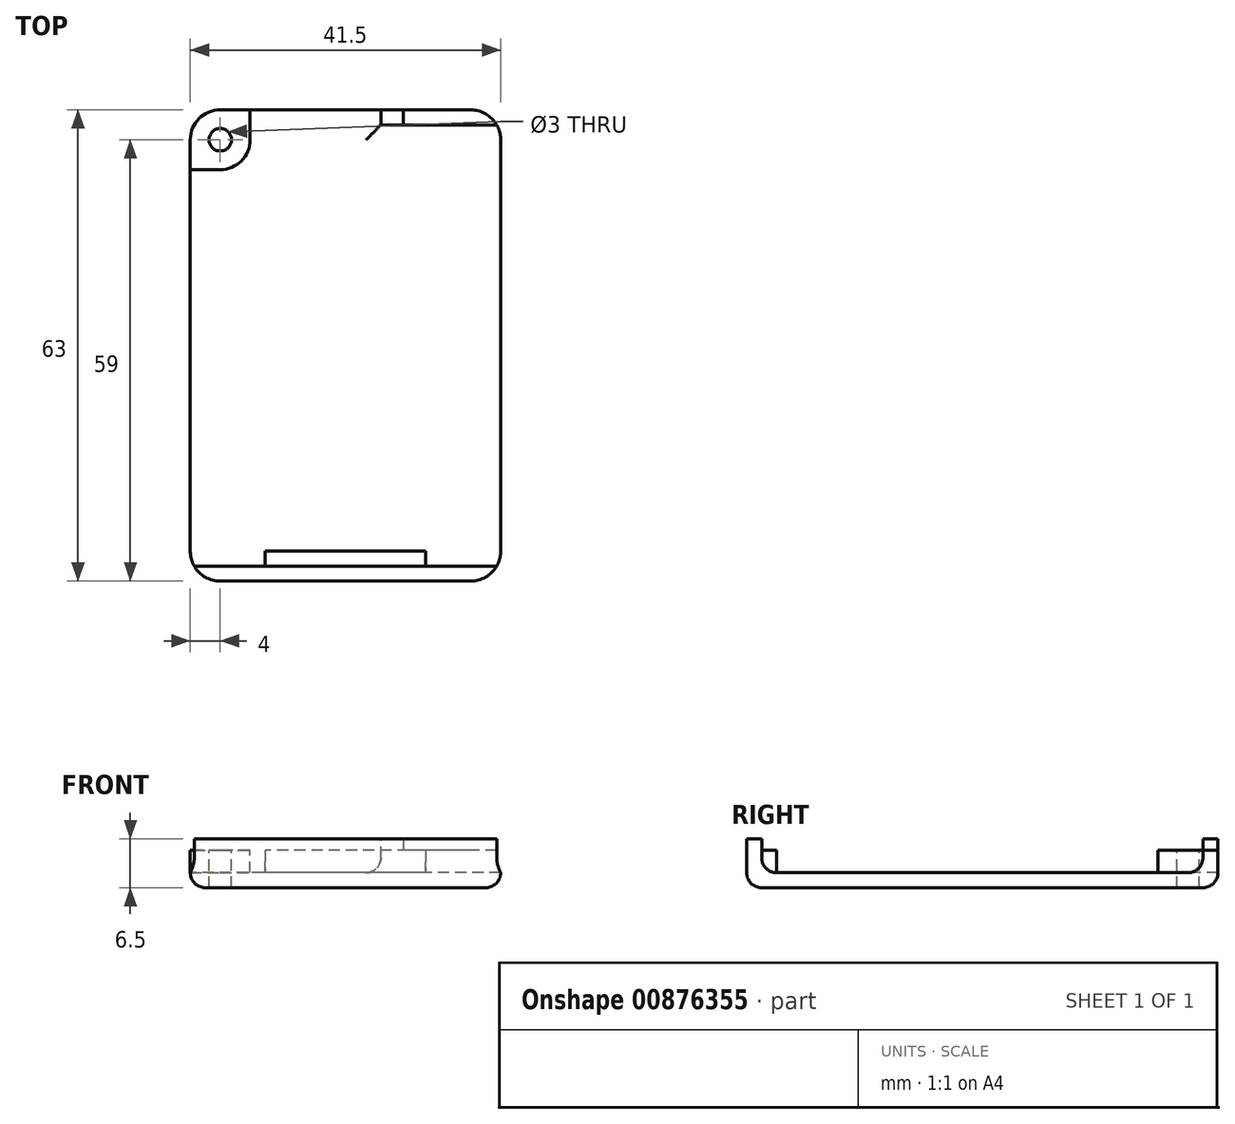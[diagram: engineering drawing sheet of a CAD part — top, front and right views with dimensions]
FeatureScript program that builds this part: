
annotation { "Feature Type Name" : "Feature", "Feature Type Description" : "" }
export const myFeature = defineFeature(function(context is Context, id is Id, definition is map)
    precondition{}
    {
        {
            var Q0;
            Q0=qCreatedBy(makeId("Top.planeOp"),FACE);
            var sketch = newSketch(context, id + "F0", { "sketchPlane" : qUnion([Q0])});
            skLineSegment(sketch, "E0.bottom", {"start": v(20.75, 31.5) * mm, "end": v(-20.75, 31.5) * mm});
            skLineSegment(sketch, "E0.top", {"start": v(20.75, -31.5) * mm, "end": v(-20.75, -31.5) * mm});
            skLineSegment(sketch, "E0.left", {"start": v(20.75, 31.5) * mm, "end": v(20.75, -31.5) * mm});
            skLineSegment(sketch, "E0.right", {"start": v(-20.75, 31.5) * mm, "end": v(-20.75, -31.5) * mm});
            skPoint(sketch, "E0.middle", {"position": v(0, 0) * mm});
            skCircle(sketch, "E1", {"center": v(-16.75, 27.5) * mm, "radius": 1.5 * mm});
            skLineSegment(sketch, "E2.bottom", {"start": v(-20.75, 31.5) * mm, "end": v(-12.75, 31.5) * mm});
            skLineSegment(sketch, "E2.top", {"start": v(-20.75, 23.5) * mm, "end": v(-12.75, 23.5) * mm});
            skLineSegment(sketch, "E2.left", {"start": v(-20.75, 31.5) * mm, "end": v(-20.75, 23.5) * mm});
            skLineSegment(sketch, "E2.right", {"start": v(-12.75, 31.5) * mm, "end": v(-12.75, 23.5) * mm});
            skLineSegment(sketch, "E3.bottom", {"start": v(20.75, 29.5) * mm, "end": v(-20.75, 29.5) * mm});
            skLineSegment(sketch, "E3.top", {"start": v(20.75, -29.5) * mm, "end": v(-20.75, -29.5) * mm});
            skLineSegment(sketch, "E3.left", {"start": v(20.75, 29.5) * mm, "end": v(20.75, -29.5) * mm});
            skLineSegment(sketch, "E3.right", {"start": v(-20.75, 29.5) * mm, "end": v(-20.75, -29.5) * mm});
            skLineSegment(sketch, "E4.bottom", {"start": v(4.75, 31.5) * mm, "end": v(20.75, 31.5) * mm});
            skLineSegment(sketch, "E4.top", {"start": v(4.75, 29.5) * mm, "end": v(20.75, 29.5) * mm});
            skLineSegment(sketch, "E4.left", {"start": v(4.75, 31.5) * mm, "end": v(4.75, 29.5) * mm});
            skLineSegment(sketch, "E4.right", {"start": v(20.75, 31.5) * mm, "end": v(20.75, 29.5) * mm});
            skLineSegment(sketch, "E5.bottom", {"start": v(4.75, 31.5) * mm, "end": v(7.75, 31.5) * mm});
            skLineSegment(sketch, "E5.top", {"start": v(4.75, 29.5) * mm, "end": v(7.75, 29.5) * mm});
            skLineSegment(sketch, "E5.right", {"start": v(7.75, 31.5) * mm, "end": v(7.75, 29.5) * mm});
            skSolve(sketch);
        }
        {
            var Q0;
            {var subQ0=sQuery(id+"F0.wireOp",EDGE,"E5.right");var subQ1=sQuery(id+"F0.wireOp",EDGE,"E0.bottom");var subQ9=makeQuery(id+"F0.imprint","IMPRINT",EDGE,{"derivedFrom":subQ0});var subQ10=sQuery(id+"F0.wireOp",EDGE,"E4.left");var subQ14=makeQuery(id+"F0.imprint","IMPRINT",EDGE,{"derivedFrom":subQ10});var subQ16=sQuery(id+"F0.wireOp",EDGE,"E2.top");var subQ19=makeQuery(id+"F0.imprint","IMPRINT",EDGE,{"derivedFrom":subQ16});var subQ20=sQuery(id+"F0.wireOp",EDGE,"E0.right");var subQ29=sQuery(id+"F0.wireOp",EDGE,"E0.top");var subQ32=makeQuery(id+"F0.imprint","INTERSECT",VERTEX,{"derivedFrom":[subQ1,subQ20]});Q0=qUnion([makeQuery(id+"F0.imprint","IMPRINT",FACE,{"disambiguationData":[TD([[makeQuery(id+"F0.imprint","IMPRINT",EDGE,{"disambiguationData":[TD([[subQ32,1.0]])],"derivedFrom":subQ1}),1.0]])]}),makeQuery(id+"F0.imprint","IMPRINT",FACE,{"disambiguationData":[TD([[makeQuery(id+"F0.imprint","IMPRINT",EDGE,{"derivedFrom":sQuery(id+"F0.wireOp",EDGE,"E1")}),-1.0]])]}),makeQuery(id+"F0.imprint","IMPRINT",FACE,{"disambiguationData":[TD([[makeQuery(id+"F0.imprint","IMPRINT",EDGE,{"derivedFrom":subQ29}),-1.0]])]}),makeQuery(id+"F0.imprint","IMPRINT",FACE,{"disambiguationData":[TD([[subQ14,-1.0]])]}),makeQuery(id+"F0.imprint","IMPRINT",FACE,{"disambiguationData":[TD([[subQ19,-1.0]])]}),makeQuery(id+"F0.imprint","IMPRINT",FACE,{"disambiguationData":[TD([[subQ14,1.0]])]}),makeQuery(id+"F0.imprint","IMPRINT",FACE,{"disambiguationData":[TD([[subQ9,1.0]])]})]);}
            extrude(context, id + "F1", {"entities" : qUnion([Q0]), "oppositeDirection" : true, "depth" : 5 * mm, "offsetDistance" : 25 * mm});
        }
        {
            var Q0;
            {var subQ1=sQuery(id+"F0.wireOp",EDGE,"E2.top");Q0=makeQuery(id+"F0.imprint","IMPRINT",FACE,{"disambiguationData":[TD([[makeQuery(id+"F0.imprint","IMPRINT",EDGE,{"derivedFrom":subQ1}),-1.0]])]});}
            var Q1;
            {var subQ0=sQuery(id+"F0.wireOp",EDGE,"E4.left");Q1=makeQuery(id+"F0.imprint","IMPRINT",FACE,{"disambiguationData":[TD([[makeQuery(id+"F0.imprint","IMPRINT",EDGE,{"derivedFrom":subQ0}),-1.0]])]});}
            extrude(context, id + "F2", {"entities" : qUnion([Q0, Q1]), "operationType" : NewBodyOperationType.REMOVE, "oppositeDirection" : true, "depth" : 3 * mm, "offsetDistance" : 25 * mm});
        }
        {
            var Q0;
            Q0=makeQuery(id+"F2.boolean.opBoolean","COPY",FACE,{"derivedFrom":makeQuery(id+"F2.opExtrude","SWEPT_FACE",FACE,{"disambiguationData":[OSD([sQuery(id+"F0.wireOp",EDGE,"E3.top")])]})});
            var sketch = newSketch(context, id + "F3", { "sketchPlane" : qUnion([Q0])});
            skLineSegment(sketch, "E6.bottom", {"start": v(-10.75, 0) * mm, "end": v(10.75, 0) * mm});
            skLineSegment(sketch, "E6.top", {"start": v(-10.75, -3) * mm, "end": v(10.75, -3) * mm});
            skLineSegment(sketch, "E6.left", {"start": v(-10.75, 0) * mm, "end": v(-10.75, -3) * mm});
            skLineSegment(sketch, "E6.right", {"start": v(10.75, 0) * mm, "end": v(10.75, -3) * mm});
            skSolve(sketch);
        }
        {
            var Q0;
            Q0 = qSketchRegion(id + "F3", true);
            extrude(context, id + "F4", {"entities" : qUnion([Q0]), "operationType" : NewBodyOperationType.ADD, "depth" : 2 * mm, "offsetDistance" : 25 * mm});
        }
        {
            var Q0;
            {var subQ0=sQuery(id+"F0.wireOp",EDGE,"E4.left");Q0=makeQuery(id+"F0.imprint","IMPRINT",FACE,{"disambiguationData":[TD([[makeQuery(id+"F0.imprint","IMPRINT",EDGE,{"derivedFrom":subQ0}),1.0]])]});}
            extrude(context, id + "F5", {"entities" : qUnion([Q0]), "operationType" : NewBodyOperationType.ADD, "depth" : 1.5 * mm, "offsetDistance" : 25 * mm});
        }
        {
            var Q0;
            {var subQ0=sQuery(id+"F0.wireOp",EDGE,"E0.top");Q0=makeQuery(id+"F0.imprint","IMPRINT",FACE,{"disambiguationData":[TD([[makeQuery(id+"F0.imprint","IMPRINT",EDGE,{"derivedFrom":subQ0}),-1.0]])]});}
            extrude(context, id + "F6", {"entities" : qUnion([Q0]), "operationType" : NewBodyOperationType.ADD, "depth" : 1.5 * mm, "offsetDistance" : 25 * mm});
        }
        {
            var Q0;
            Q0=makeQuery(id+"F2.boolean.opBoolean","COPY",EDGE,{"derivedFrom":makeQuery(id+"F2.opExtrude","SWEPT_EDGE",EDGE,{"disambiguationData":[OSD([sQuery(id+"F0.wireOp",EDGE,"E2.top"),sQuery(id+"F0.wireOp",EDGE,"E2.right")])]})});
            var Q1;
            Q1=makeQuery(id+"F2.boolean.opBoolean","COPY",EDGE,{"derivedFrom":makeQuery(id+"F2.opExtrude","SWEPT_EDGE",EDGE,{"disambiguationData":[OSD([sQuery(id+"F0.wireOp",EDGE,"E0.right"),sQuery(id+"F0.wireOp",EDGE,"E2.top")])]})});
            var Q2;
            Q2=makeQuery(id+"F2.boolean.opBoolean","COPY",EDGE,{"derivedFrom":makeQuery(id+"F2.opExtrude","SWEPT_EDGE",EDGE,{"disambiguationData":[OSD([sQuery(id+"F0.wireOp",EDGE,"E0.bottom"),sQuery(id+"F0.wireOp",EDGE,"E2.right")])]})});
            var Q3;
            Q3=makeQuery(id+"F1.opExtrude","SWEPT_EDGE",EDGE,{"disambiguationData":[OSD([sQuery(id+"F0.wireOp",EDGE,"E0.bottom"),sQuery(id+"F0.wireOp",EDGE,"E0.right")])]});
            var Q4;
            {var subQ0=sQuery(id+"F0.wireOp",EDGE,"E0.right");var subQ1=sQuery(id+"F0.wireOp",EDGE,"E0.top");Q4=makeQuery(id+"F6.boolean.opBoolean","MERGE",EDGE,{"derivedFrom":[makeQuery(id+"F1.opExtrude","SWEPT_EDGE",EDGE,{"disambiguationData":[OSD([subQ1,subQ0])]}),makeQuery(id+"F6.opExtrude","SWEPT_EDGE",EDGE,{"disambiguationData":[OSD([subQ1,subQ0])]})]});}
            var Q5;
            {var subQ0=sQuery(id+"F0.wireOp",EDGE,"E0.left");var subQ1=sQuery(id+"F0.wireOp",EDGE,"E0.top");Q5=makeQuery(id+"F6.boolean.opBoolean","MERGE",EDGE,{"derivedFrom":[makeQuery(id+"F1.opExtrude","SWEPT_EDGE",EDGE,{"disambiguationData":[OSD([subQ1,subQ0])]}),makeQuery(id+"F6.opExtrude","SWEPT_EDGE",EDGE,{"disambiguationData":[OSD([subQ1,subQ0])]})]});}
            var Q6;
            Q6=makeQuery(id+"F1.opExtrude","SWEPT_EDGE",EDGE,{"disambiguationData":[OSD([sQuery(id+"F0.wireOp",EDGE,"E0.bottom"),sQuery(id+"F0.wireOp",EDGE,"E0.left")])]});
            fillet(context, id + "F7", {"entities" : qUnion([Q0, Q1, Q2, Q3, Q4, Q5, Q6]), "radius" : 4 * mm, "tangentPropagation" : true, "allowEdgeOverflow" : false});
        }
        {
            var Q0;
            Q0=makeQuery(id+"F1.opExtrude","CAP_EDGE",EDGE,{"disambiguationData":[OSD([sQuery(id+"F0.wireOp",EDGE,"E0.right")])],"isStart":false});
            fillet(context, id + "F8", {"entities" : qUnion([Q0]), "radius" : 2 * mm, "tangentPropagation" : true, "allowEdgeOverflow" : false});
        }
        {
            var Q0;
            Q0=makeQuery(id+"F4.opExtrude","CAP_EDGE",EDGE,{"disambiguationData":[OSD([sQuery(id+"F3.wireOp",EDGE,"E6.top")])],"isStart":false});
            var Q1;
            Q1=makeQuery(id+"F4.opExtrude","SWEPT_EDGE",EDGE,{"disambiguationData":[OSD([sQuery(id+"F0.wireOp",EDGE,"E3.top"),sQuery(id+"F3.wireOp",EDGE,"E6.top"),sQuery(id+"F3.wireOp",EDGE,"E6.left")])]});
            var Q2;
            Q2=makeQuery(id+"F4.opExtrude","SWEPT_EDGE",EDGE,{"disambiguationData":[OSD([sQuery(id+"F0.wireOp",EDGE,"E3.top"),sQuery(id+"F3.wireOp",EDGE,"E6.top"),sQuery(id+"F3.wireOp",EDGE,"E6.right")])]});
            var Q3;
            {var subQ0=sQuery(id+"F0.wireOp",EDGE,"E0.right");var subQ1=sQuery(id+"F0.wireOp",EDGE,"E3.top");Q3=makeQuery(id+"F4.boolean.opBoolean","SPLIT",EDGE,{"disambiguationData":[TD([makeQuery(id+"F1.opExtrude","SWEPT_FACE",FACE,{"disambiguationData":[OSD([subQ0])]})])],"derivedFrom":makeQuery(id+"F2.boolean.opBoolean","COPY",EDGE,{"derivedFrom":makeQuery(id+"F2.opExtrude","CAP_EDGE",EDGE,{"disambiguationData":[OSD([subQ1])],"isStart":false})})});}
            var Q4;
            {var subQ0=sQuery(id+"F0.wireOp",EDGE,"E0.left");var subQ1=sQuery(id+"F0.wireOp",EDGE,"E3.top");Q4=makeQuery(id+"F4.boolean.opBoolean","SPLIT",EDGE,{"disambiguationData":[TD([makeQuery(id+"F1.opExtrude","SWEPT_FACE",FACE,{"disambiguationData":[OSD([subQ0])]})])],"derivedFrom":makeQuery(id+"F2.boolean.opBoolean","COPY",EDGE,{"derivedFrom":makeQuery(id+"F2.opExtrude","CAP_EDGE",EDGE,{"disambiguationData":[OSD([subQ1])],"isStart":false})})});}
            var Q5;
            Q5=makeQuery(id+"F2.boolean.opBoolean","COPY",EDGE,{"derivedFrom":makeQuery(id+"F2.opExtrude","CAP_EDGE",EDGE,{"disambiguationData":[OSD([sQuery(id+"F0.wireOp",EDGE,"E3.bottom")])],"isStart":false})});
            var Q6;
            {var subQ0=sQuery(id+"F0.wireOp",EDGE,"E2.top");var subQ1=sQuery(id+"F0.wireOp",EDGE,"E0.right");Q6=makeQuery(id+"F7.opFillet","BLEND_EDGE",EDGE,{"blendedFrom":[makeQuery(id+"F2.boolean.opBoolean","COPY",EDGE,{"derivedFrom":makeQuery(id+"F2.opExtrude","SWEPT_EDGE",EDGE,{"disambiguationData":[OSD([subQ1,subQ0])]})}),makeQuery(id+"F2.boolean.opBoolean","COPY",FACE,{"derivedFrom":makeQuery(id+"F2.opExtrude","CAP_FACE",FACE,{"disambiguationData":[OSD([sQuery(id+"F0.wireOp",EDGE,"E0.bottom"),sQuery(id+"F0.wireOp",EDGE,"E0.left"),subQ1,subQ0,sQuery(id+"F0.wireOp",EDGE,"E2.right"),sQuery(id+"F0.wireOp",EDGE,"E3.bottom"),sQuery(id+"F0.wireOp",EDGE,"E3.top"),sQuery(id+"F0.wireOp",EDGE,"E4.left")])],"isStart":false})})],"blendedInto":[makeQuery(id+"F2.boolean.opBoolean","COPY",FACE,{"derivedFrom":makeQuery(id+"F2.opExtrude","CAP_FACE",FACE,{"disambiguationData":[OSD([sQuery(id+"F0.wireOp",EDGE,"E0.bottom"),sQuery(id+"F0.wireOp",EDGE,"E0.left"),subQ1,subQ0,sQuery(id+"F0.wireOp",EDGE,"E2.right"),sQuery(id+"F0.wireOp",EDGE,"E3.bottom"),sQuery(id+"F0.wireOp",EDGE,"E3.top"),sQuery(id+"F0.wireOp",EDGE,"E4.left")])],"isStart":false})})]});}
            var Q7;
            Q7=makeQuery(id+"F2.boolean.opBoolean","COPY",EDGE,{"derivedFrom":makeQuery(id+"F2.opExtrude","CAP_EDGE",EDGE,{"disambiguationData":[OSD([sQuery(id+"F0.wireOp",EDGE,"E4.left")])],"isStart":false})});
            fillet(context, id + "F9", {"entities" : qUnion([Q0, Q1, Q2, Q3, Q4, Q5, Q6, Q7]), "radius" : 2 * mm, "tangentPropagation" : true, "allowEdgeOverflow" : false});
        }
    });
